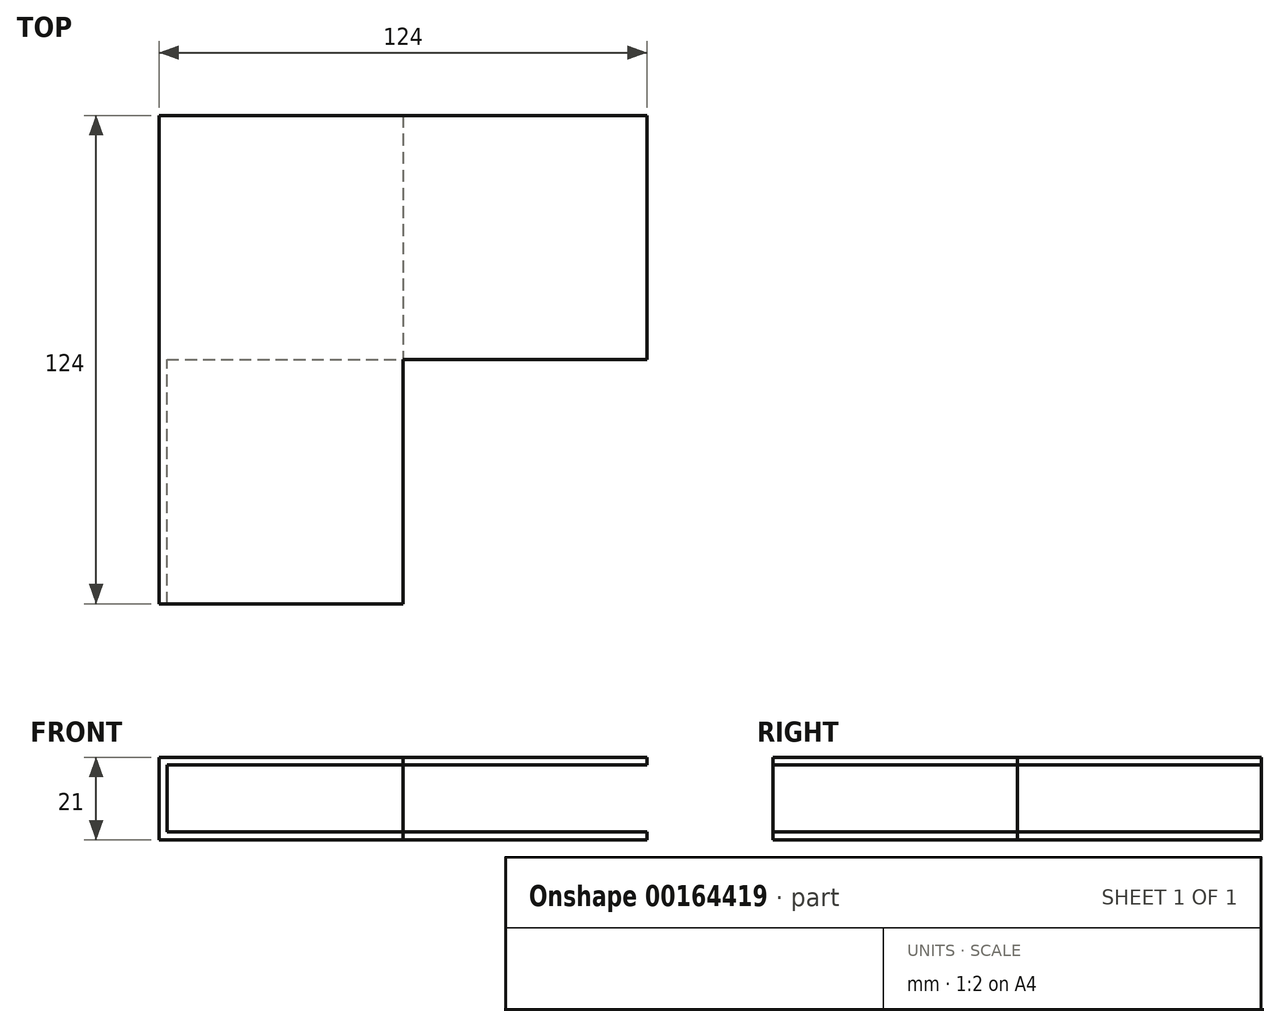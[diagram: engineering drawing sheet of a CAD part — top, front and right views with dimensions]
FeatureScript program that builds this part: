
annotation { "Feature Type Name" : "Feature", "Feature Type Description" : "" }
export const myFeature = defineFeature(function(context is Context, id is Id, definition is map)
    precondition{}
    {
        {
            var Q0;
            Q0=qCreatedBy(makeId("Top.planeOp"),FACE);
            var sketch = newSketch(context, id + "F0", { "sketchPlane" : qUnion([Q0])});
            skLineSegment(sketch, "E0.bottom", {"start": v(31, -31) * mm, "end": v(-31, -31) * mm});
            skLineSegment(sketch, "E0.top", {"start": v(31, 31) * mm, "end": v(-31, 31) * mm});
            skLineSegment(sketch, "E0.left", {"start": v(31, -31) * mm, "end": v(31, 31) * mm});
            skLineSegment(sketch, "E0.right", {"start": v(-31, -31) * mm, "end": v(-31, 31) * mm});
            skPoint(sketch, "E0.middle", {"position": v(0, 0) * mm});
            skLineSegment(sketch, "E1", {"start": v(31, 31) * mm, "end": v(93, 31) * mm});
            skLineSegment(sketch, "E2", {"start": v(31, -31) * mm, "end": v(93, -31) * mm});
            skLineSegment(sketch, "E3", {"start": v(93, -31) * mm, "end": v(93, -93) * mm});
            skLineSegment(sketch, "E4", {"start": v(93, 31) * mm, "end": v(93, -31) * mm});
            skLineSegment(sketch, "E5", {"start": v(-31, -31) * mm, "end": v(-31, -93) * mm});
            skLineSegment(sketch, "E6", {"start": v(-31, -93) * mm, "end": v(93, -93) * mm});
            skLineSegment(sketch, "E7", {"start": v(31, -31) * mm, "end": v(31, -93) * mm});
            skSolve(sketch);
        }
        {
            var Q0;
            Q0=makeQuery(id+"F0.imprint","IMPRINT",FACE,{"disambiguationData":[TD([[makeQuery(id+"F0.imprint","IMPRINT",EDGE,{"derivedFrom":sQuery(id+"F0.wireOp",EDGE,"E0.left")}),-1.0]])]});
            var Q1;
            Q1=makeQuery(id+"F0.imprint","IMPRINT",FACE,{"disambiguationData":[TD([[makeQuery(id+"F0.imprint","IMPRINT",EDGE,{"derivedFrom":sQuery(id+"F0.wireOp",EDGE,"E0.bottom")}),-1.0]])]});
            var Q2;
            Q2=makeQuery(id+"F0.imprint","IMPRINT",FACE,{"disambiguationData":[TD([[makeQuery(id+"F0.imprint","IMPRINT",EDGE,{"derivedFrom":sQuery(id+"F0.wireOp",EDGE,"E0.bottom")}),1.0]])]});
            extrude(context, id + "F1", {"entities" : qUnion([Q0, Q1, Q2]), "depth" : 21 * mm});
        }
        {
            var Q0;
            Q0=makeQuery(id+"F1.opExtrude","SWEPT_FACE",FACE,{"disambiguationData":[OSD([sQuery(id+"F0.wireOp",EDGE,"E7")])]});
            var sketch = newSketch(context, id + "F2", { "sketchPlane" : qUnion([Q0])});
            skLineSegment(sketch, "E8", {"start": v(-93, 21) * mm, "end": v(-93, 19) * mm});
            skLineSegment(sketch, "E9", {"start": v(-93, 0) * mm, "end": v(-93, 2) * mm});
            skLineSegment(sketch, "E10", {"start": v(-93, 19) * mm, "end": v(-31, 19) * mm});
            skLineSegment(sketch, "E11", {"start": v(-93, 2) * mm, "end": v(-31, 2) * mm});
            skLineSegment(sketch, "E12", {"start": v(-31, 2) * mm, "end": v(-31, 0) * mm});
            skLineSegment(sketch, "E13", {"start": v(-31, 0) * mm, "end": v(-93, 0) * mm});
            skLineSegment(sketch, "E14", {"start": v(-93, 21) * mm, "end": v(-31, 21) * mm});
            skSolve(sketch);
        }
        {
            var Q0;
            {var subQ0=sQuery(id+"F2.wireOp",EDGE,"E10");Q0=makeQuery(id+"F2.imprint","IMPRINT",FACE,{"disambiguationData":[TD([[makeQuery(id+"F2.imprint","IMPRINT",EDGE,{"derivedFrom":subQ0}),-1.0]])]});}
            extrude(context, id + "F3", {"entities" : qUnion([Q0]), "operationType" : NewBodyOperationType.REMOVE, "oppositeDirection" : true, "depth" : 60 * mm});
        }
        {
            var Q0;
            Q0=makeQuery(id+"F1.opExtrude","SWEPT_FACE",FACE,{"disambiguationData":[OSD([sQuery(id+"F0.wireOp",EDGE,"E4")])]});
            var sketch = newSketch(context, id + "F4", { "sketchPlane" : qUnion([Q0])});
            skLineSegment(sketch, "E15", {"start": v(31, 21) * mm, "end": v(31, 19) * mm});
            skLineSegment(sketch, "E16", {"start": v(31, 0) * mm, "end": v(31, 2) * mm});
            skLineSegment(sketch, "E17", {"start": v(31, 19) * mm, "end": v(-31, 19) * mm});
            skLineSegment(sketch, "E18", {"start": v(31, 2) * mm, "end": v(-31, 2) * mm});
            skLineSegment(sketch, "E19", {"start": v(-31, 2) * mm, "end": v(-31, 19) * mm});
            skLineSegment(sketch, "E20", {"start": v(31, 19) * mm, "end": v(29, 19) * mm});
            skLineSegment(sketch, "E21", {"start": v(29, 19) * mm, "end": v(29, 2) * mm});
            skSolve(sketch);
        }
        {
            var Q0;
            Q0=makeQuery(id+"F4.imprint","IMPRINT",FACE,{"disambiguationData":[TD([[makeQuery(id+"F4.imprint","IMPRINT",EDGE,{"derivedFrom":sQuery(id+"F4.wireOp",EDGE,"E17")}),1.0]])]});
            extrude(context, id + "F5", {"entities" : qUnion([Q0]), "operationType" : NewBodyOperationType.REMOVE, "oppositeDirection" : true, "depth" : 62 * mm});
        }
    });
